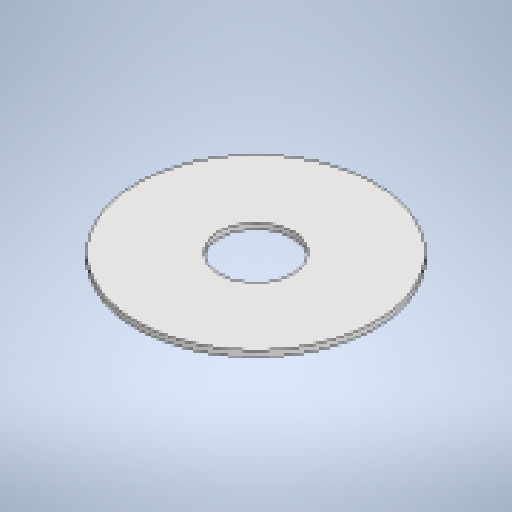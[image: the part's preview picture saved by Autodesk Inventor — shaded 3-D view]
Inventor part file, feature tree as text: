
AUTODESK INVENTOR PART (.ipt)
format: ipt  version: 2025 (Build 290162010, 162A)  size: 172,032 bytes
history: native  units: mm
features: extrude x2, other x2, sketch x2
ambient origin geometry x8: Origin, YZ Plane, XZ Plane, XY Plane, X Axis, Y Axis, Z Axis, Center Point
bodies: Solid1 (feature_tree)
feature tree (6):
  extrude  "Extrusion1"  Depth=10.0mm TaperAngle=0.0deg
  extrude  "Extrusion3"  Depth=10.0mm
  other  "A-Side Definition"
  sketch  "Sketch1"  dims[d0=390.0mm d2=10.0mm d3=0.0mm]
  sketch  "Sketch3"  dims[d4=126.0mm d13=10.0mm d14=5.0mm d15=82.5mm d16=0.0mm d17=0.0mm]
  other  "Definition1"
